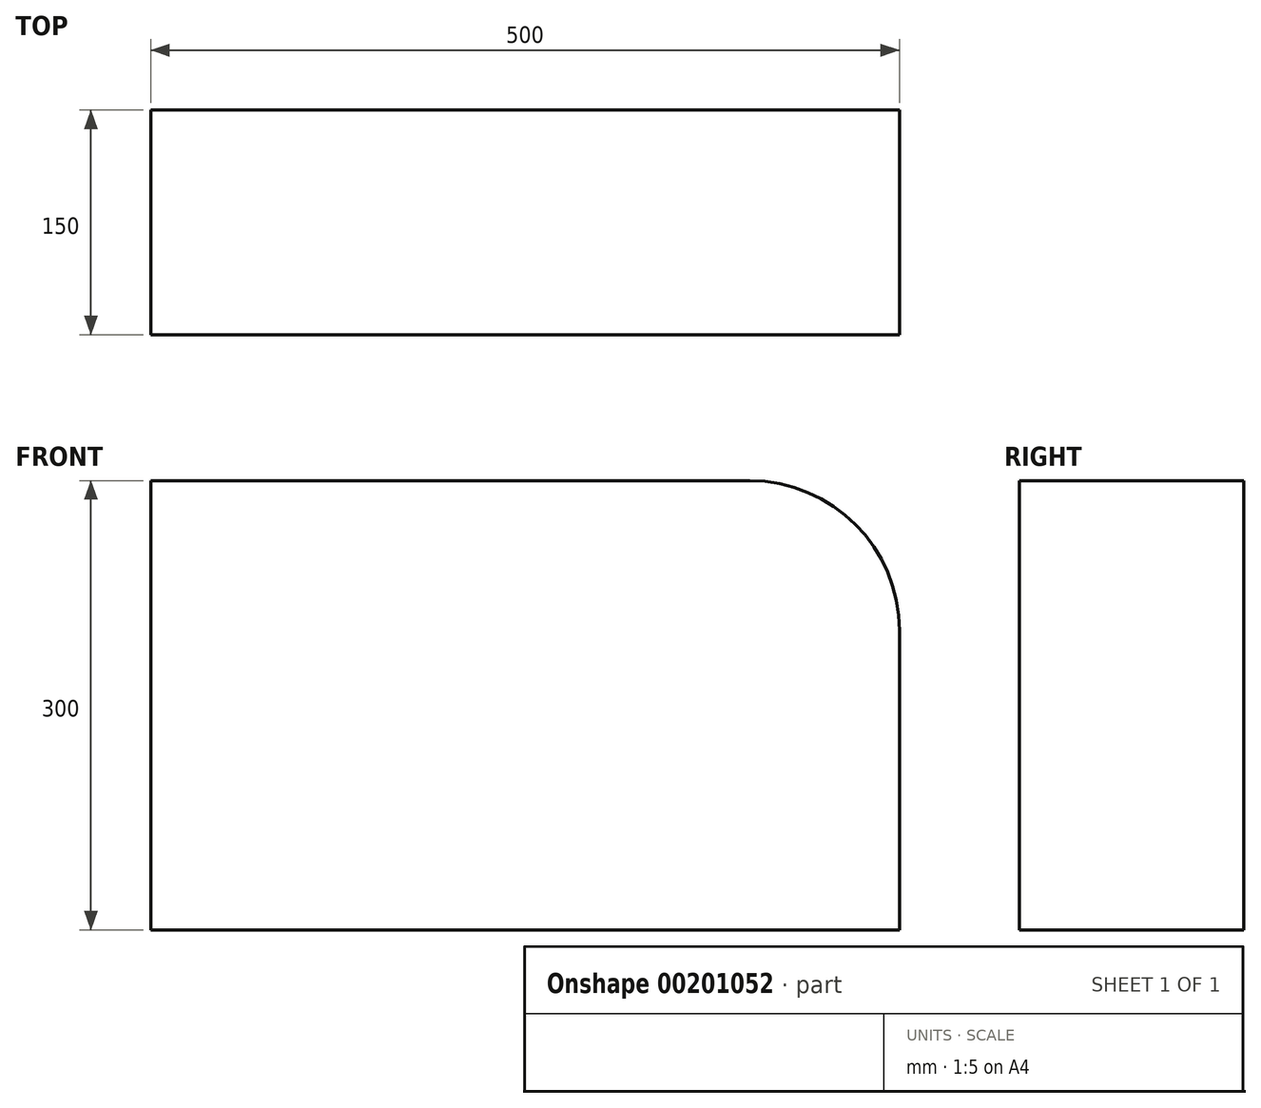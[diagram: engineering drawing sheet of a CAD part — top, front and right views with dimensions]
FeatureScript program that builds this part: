
annotation { "Feature Type Name" : "Feature", "Feature Type Description" : "" }
export const myFeature = defineFeature(function(context is Context, id is Id, definition is map)
    precondition{}
    {
        {
            var Q0;
            Q0=qCreatedBy(makeId("Top.planeOp"),FACE);
            var sketch = newSketch(context, id + "F0", { "sketchPlane" : qUnion([Q0])});
            skLineSegment(sketch, "E0.bottom", {"start": v(-233.45, 84.96) * mm, "end": v(266.55, 84.96) * mm});
            skLineSegment(sketch, "E0.top", {"start": v(-233.45, -65.04) * mm, "end": v(266.55, -65.04) * mm});
            skLineSegment(sketch, "E0.left", {"start": v(-233.45, 84.96) * mm, "end": v(-233.45, -65.04) * mm});
            skLineSegment(sketch, "E0.right", {"start": v(266.55, 84.96) * mm, "end": v(266.55, -65.04) * mm});
            skSolve(sketch);
        }
        {
            var Q0;
            Q0=makeQuery(id+"F0.imprint","IMPRINT",FACE,{"disambiguationData":[TD([[makeQuery(id+"F0.imprint","IMPRINT",EDGE,{"derivedFrom":sQuery(id+"F0.wireOp",EDGE,"E0.bottom")}),-1.0]])]});
            extrude(context, id + "F1", {"entities" : qUnion([Q0]), "depth" : 300 * mm});
        }
        {
            var Q0;
            Q0=makeQuery(id+"F1.opExtrude","CAP_EDGE",EDGE,{"disambiguationData":[OSD([sQuery(id+"F0.wireOp",EDGE,"E0.right")])],"isStart":false});
            fillet(context, id + "F2", {"entities" : qUnion([Q0]), "radius" : 100 * mm, "tangentPropagation" : true, "allowEdgeOverflow" : false});
        }
    });
